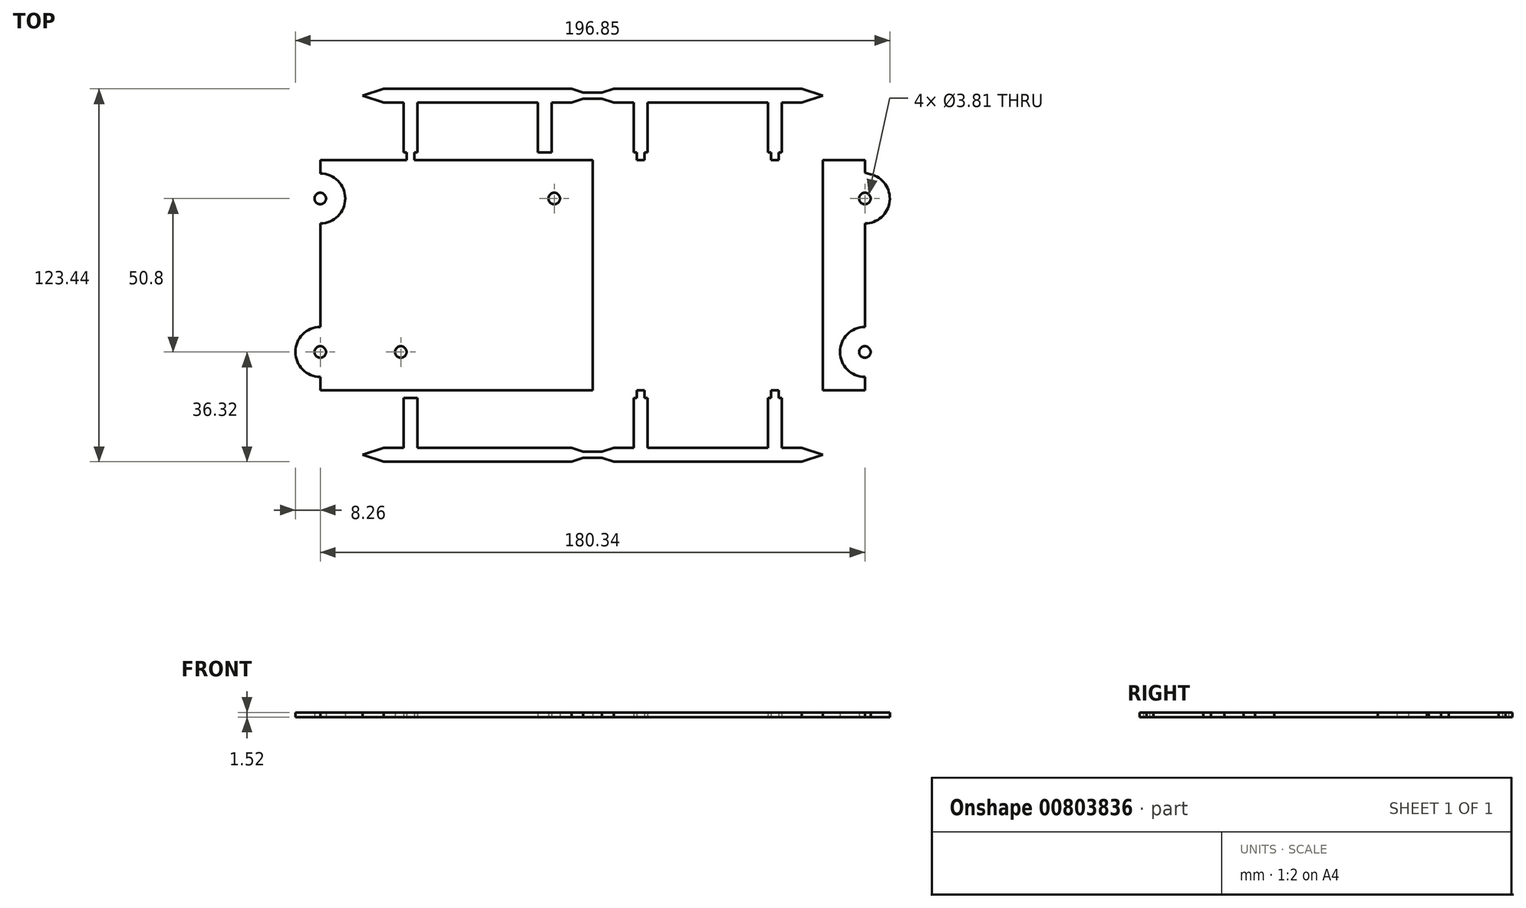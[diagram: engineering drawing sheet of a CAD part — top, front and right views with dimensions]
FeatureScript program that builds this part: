
annotation { "Feature Type Name" : "Feature", "Feature Type Description" : "" }
export const myFeature = defineFeature(function(context is Context, id is Id, definition is map)
    precondition{}
    {
        {
            var Q0;
            Q0=qCreatedBy(makeId("Top.planeOp"),FACE);
            var sketch = newSketch(context, id + "F0", { "sketchPlane" : qUnion([Q0])});
            skLineSegment(sketch, "E0.bottom", {"start": v(38.1, 38.1) * mm, "end": v(-38.1, 38.1) * mm});
            skLineSegment(sketch, "E0.top", {"start": v(38.1, -38.1) * mm, "end": v(-38.1, -38.1) * mm});
            skLineSegment(sketch, "E0.left", {"start": v(38.1, 38.1) * mm, "end": v(38.1, -38.1) * mm});
            skPoint(sketch, "E0.middle", {"position": v(0, 0) * mm});
            skLineSegment(sketch, "E1.bottom", {"start": v(31.75, 31.75) * mm, "end": v(-31.75, 31.75) * mm, "construction": true});
            skLineSegment(sketch, "E1.top", {"start": v(31.75, -31.75) * mm, "end": v(-31.75, -31.75) * mm, "construction": true});
            skLineSegment(sketch, "E1.left", {"start": v(31.75, 31.75) * mm, "end": v(31.75, -31.75) * mm, "construction": true});
            skLineSegment(sketch, "E1.right", {"start": v(-31.75, 31.75) * mm, "end": v(-31.75, -31.75) * mm, "construction": true});
            skLineSegment(sketch, "E2.bottom", {"start": v(-19.18, -31.75) * mm, "end": v(-12.57, -31.75) * mm});
            skLineSegment(sketch, "E2.top", {"start": v(-19.18, -30.23) * mm, "end": v(-12.57, -30.23) * mm});
            skLineSegment(sketch, "E2.left", {"start": v(-19.18, -31.75) * mm, "end": v(-19.18, -30.23) * mm});
            skLineSegment(sketch, "E2.right", {"start": v(-12.57, -31.75) * mm, "end": v(-12.57, -30.23) * mm});
            skPoint(sketch, "E3", {"position": v(-15.88, -31.75) * mm});
            skLineSegment(sketch, "E4.0", {"start": v(-19.43, -29.97) * mm, "end": v(-12.32, -29.97) * mm});
            skLineSegment(sketch, "E4.1", {"start": v(-19.43, -32) * mm, "end": v(-19.43, -29.97) * mm});
            skLineSegment(sketch, "E4.2", {"start": v(-19.43, -32) * mm, "end": v(-12.32, -32) * mm});
            skLineSegment(sketch, "E4.3", {"start": v(-12.32, -32) * mm, "end": v(-12.32, -29.97) * mm});
            skLineSegment(sketch, "E5.MirrorCS", {"start": v(19.43, -29.97) * mm, "end": v(12.32, -29.97) * mm});
            skLineSegment(sketch, "E6.MirrorCS", {"start": v(19.43, -32) * mm, "end": v(19.43, -29.97) * mm});
            skLineSegment(sketch, "E7.MirrorCS", {"start": v(19.43, -32) * mm, "end": v(12.32, -32) * mm});
            skLineSegment(sketch, "E8.MirrorCS", {"start": v(12.32, -32) * mm, "end": v(12.32, -29.97) * mm});
            skLineSegment(sketch, "E9.MirrorCS", {"start": v(-19.43, 32) * mm, "end": v(-19.43, 29.97) * mm});
            skLineSegment(sketch, "E10.MirrorCS", {"start": v(-19.43, 29.97) * mm, "end": v(-12.32, 29.97) * mm});
            skLineSegment(sketch, "E11.MirrorCS", {"start": v(-12.32, 32) * mm, "end": v(-12.32, 29.97) * mm});
            skLineSegment(sketch, "E12.MirrorCS", {"start": v(-19.43, 32) * mm, "end": v(-12.32, 32) * mm});
            skLineSegment(sketch, "E13.MirrorCS", {"start": v(19.43, 29.97) * mm, "end": v(12.32, 29.97) * mm});
            skLineSegment(sketch, "E14.MirrorCS", {"start": v(19.43, 32) * mm, "end": v(19.43, 29.97) * mm});
            skLineSegment(sketch, "E15.MirrorCS", {"start": v(19.43, 32) * mm, "end": v(12.32, 32) * mm});
            skLineSegment(sketch, "E16.MirrorCS", {"start": v(12.32, 32) * mm, "end": v(12.32, 29.97) * mm});
            skLineSegment(sketch, "E17.bottom", {"start": v(-31.75, -19.18) * mm, "end": v(-30.23, -19.18) * mm});
            skLineSegment(sketch, "E17.top", {"start": v(-31.75, -12.57) * mm, "end": v(-30.23, -12.57) * mm});
            skLineSegment(sketch, "E17.left", {"start": v(-31.75, -19.18) * mm, "end": v(-31.75, -12.57) * mm});
            skLineSegment(sketch, "E17.right", {"start": v(-30.23, -19.18) * mm, "end": v(-30.23, -12.57) * mm});
            skPoint(sketch, "E18", {"position": v(-31.75, -15.88) * mm});
            skLineSegment(sketch, "E19.0", {"start": v(-29.97, -19.43) * mm, "end": v(-29.97, -12.32) * mm});
            skLineSegment(sketch, "E19.1", {"start": v(-32, -19.43) * mm, "end": v(-29.97, -19.43) * mm});
            skLineSegment(sketch, "E19.2", {"start": v(-32, -19.43) * mm, "end": v(-32, -12.32) * mm});
            skLineSegment(sketch, "E19.3", {"start": v(-32, -12.32) * mm, "end": v(-29.97, -12.32) * mm});
            skLineSegment(sketch, "E20.MirrorCS", {"start": v(-32, 19.43) * mm, "end": v(-32, 12.32) * mm});
            skLineSegment(sketch, "E21.MirrorCS", {"start": v(-32, 12.32) * mm, "end": v(-29.97, 12.32) * mm});
            skLineSegment(sketch, "E22.MirrorCS", {"start": v(-29.97, 19.43) * mm, "end": v(-29.97, 12.32) * mm});
            skLineSegment(sketch, "E23.MirrorCS", {"start": v(-32, 19.43) * mm, "end": v(-29.97, 19.43) * mm});
            skLineSegment(sketch, "E24.MirrorCS", {"start": v(32, -19.43) * mm, "end": v(32, -12.32) * mm});
            skLineSegment(sketch, "E25.MirrorCS", {"start": v(32, -12.32) * mm, "end": v(29.97, -12.32) * mm});
            skLineSegment(sketch, "E26.MirrorCS", {"start": v(29.97, -19.43) * mm, "end": v(29.97, -12.32) * mm});
            skLineSegment(sketch, "E27.MirrorCS", {"start": v(32, -19.43) * mm, "end": v(29.97, -19.43) * mm});
            skLineSegment(sketch, "E28.MirrorCS", {"start": v(29.97, 19.43) * mm, "end": v(29.97, 12.32) * mm});
            skLineSegment(sketch, "E29.MirrorCS", {"start": v(32, 12.32) * mm, "end": v(29.97, 12.32) * mm});
            skLineSegment(sketch, "E30.MirrorCS", {"start": v(32, 19.43) * mm, "end": v(32, 12.32) * mm});
            skLineSegment(sketch, "E31.MirrorCS", {"start": v(32, 19.43) * mm, "end": v(29.97, 19.43) * mm});
            skLineSegment(sketch, "E32.bottom", {"start": v(-23.5, -38.1) * mm, "end": v(-20.96, -38.1) * mm});
            skLineSegment(sketch, "E32.top", {"start": v(-23.5, -40.64) * mm, "end": v(-20.96, -40.64) * mm});
            skLineSegment(sketch, "E32.left", {"start": v(-23.5, -38.1) * mm, "end": v(-23.5, -40.64) * mm});
            skLineSegment(sketch, "E32.right", {"start": v(-20.96, -38.1) * mm, "end": v(-20.96, -40.64) * mm});
            skPoint(sketch, "E33", {"position": v(-22.23, -38.1) * mm});
            skLineSegment(sketch, "E34.bottom", {"start": v(-24.51, -40.64) * mm, "end": v(-19.94, -40.64) * mm});
            skLineSegment(sketch, "E34.top", {"start": v(-24.51, -57.15) * mm, "end": v(-19.94, -57.15) * mm});
            skLineSegment(sketch, "E34.left", {"start": v(-24.51, -40.64) * mm, "end": v(-24.51, -57.15) * mm});
            skLineSegment(sketch, "E34.right", {"start": v(-19.94, -40.64) * mm, "end": v(-19.94, -57.15) * mm});
            skPoint(sketch, "E35", {"position": v(-22.23, -40.64) * mm});
            skLineSegment(sketch, "E36.MirrorCS", {"start": v(23.5, -38.1) * mm, "end": v(20.96, -38.1) * mm});
            skPoint(sketch, "E37.MirrorP", {"position": v(22.23, -38.1) * mm});
            skLineSegment(sketch, "E38.bottom", {"start": v(0, -57.15) * mm, "end": v(-31.12, -57.15) * mm});
            skLineSegment(sketch, "E38.top", {"start": v(0, -61.72) * mm, "end": v(-31.12, -61.72) * mm});
            skLineSegment(sketch, "E39", {"start": v(-38.1, -59.44) * mm, "end": v(-31.12, -57.15) * mm});
            skLineSegment(sketch, "E40", {"start": v(-38.1, -59.44) * mm, "end": v(-31.12, -61.72) * mm});
            skPoint(sketch, "E41.start.orphan", {"position": v(-31.12, -59.44) * mm});
            skLineSegment(sketch, "E42.MirrorCS", {"start": v(38.1, -38.1) * mm, "end": v(38.1, 38.1) * mm});
            skPoint(sketch, "E43.MirrorP", {"position": v(-38.1, 57.15) * mm});
            skCircle(sketch, "E44", {"center": v(-25.4, 25.4) * mm, "radius": 1.9 * mm});
            skCircle(sketch, "E45.MirrorC", {"center": v(25.4, 25.4) * mm, "radius": 1.9 * mm});
            skCircle(sketch, "E46.MirrorC", {"center": v(-25.4, -25.4) * mm, "radius": 1.9 * mm});
            skCircle(sketch, "E47.MirrorC", {"center": v(25.4, -25.4) * mm, "radius": 1.9 * mm});
            skLineSegment(sketch, "E48", {"start": v(0, 38.1) * mm, "end": v(0, -38.1) * mm, "construction": true});
            skLineSegment(sketch, "E49", {"start": v(0, -38.1) * mm, "end": v(0, -79.98) * mm, "construction": true});
            skLineSegment(sketch, "E50.MirrorCS", {"start": v(24.51, -40.64) * mm, "end": v(19.94, -40.64) * mm});
            skLineSegment(sketch, "E51.MirrorCS", {"start": v(23.5, -40.64) * mm, "end": v(20.96, -40.64) * mm});
            skLineSegment(sketch, "E52.MirrorCS", {"start": v(23.5, -38.1) * mm, "end": v(23.5, -40.64) * mm});
            skLineSegment(sketch, "E53.MirrorCS", {"start": v(20.96, -38.1) * mm, "end": v(20.96, -40.64) * mm});
            skLineSegment(sketch, "E54.MirrorCS", {"start": v(24.51, -57.15) * mm, "end": v(19.94, -57.15) * mm});
            skPoint(sketch, "E55.MirrorP", {"position": v(22.23, -40.64) * mm});
            skLineSegment(sketch, "E56.MirrorCS", {"start": v(0, -57.15) * mm, "end": v(31.12, -57.15) * mm});
            skLineSegment(sketch, "E57.MirrorCS", {"start": v(38.1, -59.44) * mm, "end": v(31.12, -57.15) * mm});
            skLineSegment(sketch, "E58.MirrorCS", {"start": v(38.1, -59.44) * mm, "end": v(31.12, -61.72) * mm});
            skLineSegment(sketch, "E59.MirrorCS", {"start": v(24.51, -40.64) * mm, "end": v(24.51, -57.15) * mm});
            skLineSegment(sketch, "E60.MirrorCS", {"start": v(0, -61.72) * mm, "end": v(31.12, -61.72) * mm});
            skPoint(sketch, "E61.MirrorP", {"position": v(31.12, -59.44) * mm});
            skLineSegment(sketch, "E62.MirrorCS", {"start": v(19.94, -40.64) * mm, "end": v(19.94, -57.15) * mm});
            skLineSegment(sketch, "E63.MirrorCS", {"start": v(-23.5, 40.64) * mm, "end": v(-20.96, 40.64) * mm});
            skLineSegment(sketch, "E64.MirrorCS", {"start": v(-24.51, 40.64) * mm, "end": v(-19.94, 40.64) * mm});
            skPoint(sketch, "E65.MirrorP", {"position": v(22.23, 38.1) * mm});
            skLineSegment(sketch, "E66.MirrorCS", {"start": v(24.51, 40.64) * mm, "end": v(19.94, 40.64) * mm});
            skLineSegment(sketch, "E67.MirrorCS", {"start": v(23.5, 40.64) * mm, "end": v(20.96, 40.64) * mm});
            skPoint(sketch, "E68.MirrorP", {"position": v(-22.23, 38.1) * mm});
            skPoint(sketch, "E69.MirrorP", {"position": v(22.23, 40.64) * mm});
            skPoint(sketch, "E70.MirrorP", {"position": v(-22.23, 40.64) * mm});
            skLineSegment(sketch, "E71.MirrorCS", {"start": v(24.51, 57.15) * mm, "end": v(19.94, 57.15) * mm});
            skLineSegment(sketch, "E72.MirrorCS", {"start": v(-24.51, 57.15) * mm, "end": v(-19.94, 57.15) * mm});
            skLineSegment(sketch, "E73.MirrorCS", {"start": v(24.51, 40.64) * mm, "end": v(24.51, 57.15) * mm});
            skLineSegment(sketch, "E74.MirrorCS", {"start": v(-24.51, 40.64) * mm, "end": v(-24.51, 57.15) * mm});
            skLineSegment(sketch, "E75.MirrorCS", {"start": v(-19.94, 40.64) * mm, "end": v(-19.94, 57.15) * mm});
            skLineSegment(sketch, "E76.MirrorCS", {"start": v(0, 61.72) * mm, "end": v(31.12, 61.72) * mm});
            skLineSegment(sketch, "E77.MirrorCS", {"start": v(-38.1, 59.44) * mm, "end": v(-31.12, 61.72) * mm});
            skLineSegment(sketch, "E78.MirrorCS", {"start": v(19.94, 40.64) * mm, "end": v(19.94, 57.15) * mm});
            skPoint(sketch, "E79.MirrorP", {"position": v(-31.12, 59.44) * mm});
            skLineSegment(sketch, "E80.MirrorCS", {"start": v(-38.1, 59.44) * mm, "end": v(-31.12, 57.15) * mm});
            skLineSegment(sketch, "E81.MirrorCS", {"start": v(0, 57.15) * mm, "end": v(31.12, 57.15) * mm});
            skLineSegment(sketch, "E82.MirrorCS", {"start": v(38.1, 59.44) * mm, "end": v(31.12, 61.72) * mm});
            skLineSegment(sketch, "E83.MirrorCS", {"start": v(0, 61.72) * mm, "end": v(-31.12, 61.72) * mm});
            skPoint(sketch, "E84.MirrorP", {"position": v(31.12, 59.44) * mm});
            skLineSegment(sketch, "E85.MirrorCS", {"start": v(0, 57.15) * mm, "end": v(-31.12, 57.15) * mm});
            skLineSegment(sketch, "E86.MirrorCS", {"start": v(38.1, 59.44) * mm, "end": v(31.12, 57.15) * mm});
            skLineSegment(sketch, "E87.MirrorCS", {"start": v(-23.5, 38.1) * mm, "end": v(-20.96, 38.1) * mm});
            skLineSegment(sketch, "E88.MirrorCS", {"start": v(-20.96, 38.1) * mm, "end": v(-20.96, 40.64) * mm});
            skLineSegment(sketch, "E89.MirrorCS", {"start": v(-23.5, 38.1) * mm, "end": v(-23.5, 40.64) * mm});
            skLineSegment(sketch, "E90.MirrorCS", {"start": v(23.5, 38.1) * mm, "end": v(20.96, 38.1) * mm});
            skLineSegment(sketch, "E91.MirrorCS", {"start": v(20.96, 38.1) * mm, "end": v(20.96, 40.64) * mm});
            skLineSegment(sketch, "E92.MirrorCS", {"start": v(23.5, 38.1) * mm, "end": v(23.5, 40.64) * mm});
            skLineSegment(sketch, "E93", {"start": v(-38.1, -59.44) * mm, "end": v(38.1, -59.44) * mm});
            skLineSegment(sketch, "E94.0", {"start": v(-38.1, -60.45) * mm, "end": v(38.1, -60.45) * mm});
            skLineSegment(sketch, "E95.0", {"start": v(-38.1, -58.42) * mm, "end": v(38.1, -58.42) * mm});
            skLineSegment(sketch, "E96.MirrorCS", {"start": v(-38.1, 58.42) * mm, "end": v(38.1, 58.42) * mm});
            skLineSegment(sketch, "E97.MirrorCS", {"start": v(-38.1, 60.45) * mm, "end": v(38.1, 60.45) * mm});
            skLineSegment(sketch, "E98.MirrorCS", {"start": v(52.7, 38.1) * mm, "end": v(55.25, 38.1) * mm});
            skLineSegment(sketch, "E99.MirrorCS", {"start": v(52.7, 40.64) * mm, "end": v(55.25, 40.64) * mm});
            skLineSegment(sketch, "E100.MirrorCS", {"start": v(52.7, 38.1) * mm, "end": v(52.7, 40.64) * mm});
            skLineSegment(sketch, "E101.MirrorCS", {"start": v(55.25, 38.1) * mm, "end": v(55.25, 40.64) * mm});
            skLineSegment(sketch, "E102.MirrorCS", {"start": v(99.7, 40.64) * mm, "end": v(97.16, 40.64) * mm});
            skLineSegment(sketch, "E103.MirrorCS", {"start": v(99.7, 38.1) * mm, "end": v(97.16, 38.1) * mm});
            skLineSegment(sketch, "E104.MirrorCS", {"start": v(97.16, 38.1) * mm, "end": v(97.16, 40.64) * mm});
            skLineSegment(sketch, "E105.MirrorCS", {"start": v(100.71, 40.64) * mm, "end": v(96.14, 40.64) * mm});
            skLineSegment(sketch, "E106.MirrorCS", {"start": v(99.7, 38.1) * mm, "end": v(99.7, 40.64) * mm});
            skLineSegment(sketch, "E107.MirrorCS", {"start": v(51.69, 40.64) * mm, "end": v(56.26, 40.64) * mm});
            skPoint(sketch, "E108.MirrorP", {"position": v(98.43, 38.1) * mm});
            skPoint(sketch, "E109.MirrorP", {"position": v(53.98, 40.64) * mm});
            skPoint(sketch, "E110.MirrorP", {"position": v(98.43, 40.64) * mm});
            skPoint(sketch, "E111.MirrorP", {"position": v(53.98, 38.1) * mm});
            skLineSegment(sketch, "E112.MirrorCS", {"start": v(38.1, 59.44) * mm, "end": v(45.08, 57.15) * mm});
            skLineSegment(sketch, "E113.MirrorCS", {"start": v(51.69, 57.15) * mm, "end": v(56.26, 57.15) * mm});
            skLineSegment(sketch, "E114.MirrorCS", {"start": v(100.71, 57.15) * mm, "end": v(96.14, 57.15) * mm});
            skLineSegment(sketch, "E115.MirrorCS", {"start": v(38.1, 59.44) * mm, "end": v(45.08, 61.72) * mm});
            skLineSegment(sketch, "E116.MirrorCS", {"start": v(114.3, 59.44) * mm, "end": v(107.32, 61.72) * mm});
            skLineSegment(sketch, "E117.MirrorCS", {"start": v(114.3, 59.44) * mm, "end": v(107.32, 57.15) * mm});
            skLineSegment(sketch, "E118.MirrorCS", {"start": v(38.1, 38.1) * mm, "end": v(114.3, 38.1) * mm});
            skLineSegment(sketch, "E119.MirrorCS", {"start": v(114.3, 60.45) * mm, "end": v(38.1, 60.45) * mm});
            skPoint(sketch, "E120.MirrorP", {"position": v(114.3, 57.15) * mm});
            skLineSegment(sketch, "E121.MirrorCS", {"start": v(76.2, 57.15) * mm, "end": v(45.08, 57.15) * mm});
            skPoint(sketch, "E122.MirrorP", {"position": v(107.32, 59.44) * mm});
            skPoint(sketch, "E123.MirrorP", {"position": v(45.08, 59.44) * mm});
            skLineSegment(sketch, "E124.MirrorCS", {"start": v(51.69, 40.64) * mm, "end": v(51.69, 57.15) * mm});
            skLineSegment(sketch, "E125.MirrorCS", {"start": v(100.71, 40.64) * mm, "end": v(100.71, 57.15) * mm});
            skLineSegment(sketch, "E126.MirrorCS", {"start": v(56.26, 40.64) * mm, "end": v(56.26, 57.15) * mm});
            skLineSegment(sketch, "E127.MirrorCS", {"start": v(96.14, 40.64) * mm, "end": v(96.14, 57.15) * mm});
            skLineSegment(sketch, "E128.MirrorCS", {"start": v(76.2, 61.72) * mm, "end": v(45.08, 61.72) * mm});
            skLineSegment(sketch, "E129.MirrorCS", {"start": v(76.2, 61.72) * mm, "end": v(107.32, 61.72) * mm});
            skLineSegment(sketch, "E130.MirrorCS", {"start": v(114.3, 58.42) * mm, "end": v(38.1, 58.42) * mm});
            skLineSegment(sketch, "E131.MirrorCS", {"start": v(76.2, 57.15) * mm, "end": v(107.32, 57.15) * mm});
            skLineSegment(sketch, "E132.MirrorCS", {"start": v(52.7, -38.1) * mm, "end": v(55.25, -38.1) * mm});
            skLineSegment(sketch, "E133.MirrorCS", {"start": v(52.7, -40.64) * mm, "end": v(55.25, -40.64) * mm});
            skLineSegment(sketch, "E134.MirrorCS", {"start": v(99.7, -38.1) * mm, "end": v(97.16, -38.1) * mm});
            skLineSegment(sketch, "E135.MirrorCS", {"start": v(55.25, -38.1) * mm, "end": v(55.25, -40.64) * mm});
            skLineSegment(sketch, "E136.MirrorCS", {"start": v(97.16, -38.1) * mm, "end": v(97.16, -40.64) * mm});
            skLineSegment(sketch, "E137.MirrorCS", {"start": v(52.7, -38.1) * mm, "end": v(52.7, -40.64) * mm});
            skLineSegment(sketch, "E138.MirrorCS", {"start": v(99.7, -40.64) * mm, "end": v(97.16, -40.64) * mm});
            skLineSegment(sketch, "E139.MirrorCS", {"start": v(99.7, -38.1) * mm, "end": v(99.7, -40.64) * mm});
            skLineSegment(sketch, "E140.MirrorCS", {"start": v(100.71, -40.64) * mm, "end": v(96.14, -40.64) * mm});
            skLineSegment(sketch, "E141.MirrorCS", {"start": v(51.69, -40.64) * mm, "end": v(56.26, -40.64) * mm});
            skLineSegment(sketch, "E142.MirrorCS", {"start": v(38.1, -59.44) * mm, "end": v(45.08, -61.72) * mm});
            skLineSegment(sketch, "E143.MirrorCS", {"start": v(114.3, -59.44) * mm, "end": v(107.32, -61.72) * mm});
            skLineSegment(sketch, "E144.MirrorCS", {"start": v(38.1, -59.44) * mm, "end": v(45.08, -57.15) * mm});
            skLineSegment(sketch, "E145.MirrorCS", {"start": v(51.69, -57.15) * mm, "end": v(56.26, -57.15) * mm});
            skLineSegment(sketch, "E146.MirrorCS", {"start": v(114.3, -59.44) * mm, "end": v(107.32, -57.15) * mm});
            skLineSegment(sketch, "E147.MirrorCS", {"start": v(100.71, -57.15) * mm, "end": v(96.14, -57.15) * mm});
            skPoint(sketch, "E148.MirrorP", {"position": v(98.42, -40.64) * mm});
            skPoint(sketch, "E149.MirrorP", {"position": v(53.97, -38.1) * mm});
            skPoint(sketch, "E150.MirrorP", {"position": v(53.97, -40.64) * mm});
            skLineSegment(sketch, "E151.MirrorCS", {"start": v(114.3, -59.44) * mm, "end": v(38.1, -59.44) * mm});
            skLineSegment(sketch, "E152.MirrorCS", {"start": v(100.71, -40.64) * mm, "end": v(100.71, -57.15) * mm});
            skLineSegment(sketch, "E153.MirrorCS", {"start": v(38.1, -38.1) * mm, "end": v(114.3, -38.1) * mm});
            skLineSegment(sketch, "E154.MirrorCS", {"start": v(96.14, -40.64) * mm, "end": v(96.14, -57.15) * mm});
            skLineSegment(sketch, "E155.MirrorCS", {"start": v(51.69, -40.64) * mm, "end": v(51.69, -57.15) * mm});
            skPoint(sketch, "E156.MirrorP", {"position": v(98.42, -38.1) * mm});
            skPoint(sketch, "E157.MirrorP", {"position": v(107.32, -59.44) * mm});
            skLineSegment(sketch, "E158.MirrorCS", {"start": v(76.2, -38.1) * mm, "end": v(76.2, -79.98) * mm, "construction": true});
            skPoint(sketch, "E159.MirrorP", {"position": v(92.08, -31.75) * mm});
            skLineSegment(sketch, "E160.MirrorCS", {"start": v(76.2, -61.72) * mm, "end": v(45.08, -61.72) * mm});
            skLineSegment(sketch, "E161.MirrorCS", {"start": v(76.2, -61.72) * mm, "end": v(107.32, -61.72) * mm});
            skLineSegment(sketch, "E162.MirrorCS", {"start": v(76.2, -57.15) * mm, "end": v(107.32, -57.15) * mm});
            skPoint(sketch, "E163.MirrorP", {"position": v(45.08, -59.44) * mm});
            skLineSegment(sketch, "E164.MirrorCS", {"start": v(56.26, -40.64) * mm, "end": v(56.26, -57.15) * mm});
            skLineSegment(sketch, "E165.MirrorCS", {"start": v(76.2, -57.15) * mm, "end": v(45.08, -57.15) * mm});
            skLineSegment(sketch, "E166.MirrorCS", {"start": v(114.3, -60.45) * mm, "end": v(38.1, -60.45) * mm});
            skLineSegment(sketch, "E167.MirrorCS", {"start": v(114.3, -58.42) * mm, "end": v(38.1, -58.42) * mm});
            skLineSegment(sketch, "E168", {"start": v(-38.1, 38.1) * mm, "end": v(-38.1, -38.1) * mm});
            skCircle(sketch, "E169", {"center": v(-52.07, -25.4) * mm, "radius": 1.9 * mm});
            skCircle(sketch, "E170.0", {"center": v(-52.07, -25.4) * mm, "radius": 8.25 * mm});
            skLineSegment(sketch, "E171", {"start": v(-38.1, -38.1) * mm, "end": v(-53.94, -33.44) * mm});
            skCircle(sketch, "E172.MirrorC", {"center": v(-52.07, 25.4) * mm, "radius": 1.9 * mm});
            skCircle(sketch, "E173.MirrorC", {"center": v(-52.07, 25.4) * mm, "radius": 8.25 * mm});
            skLineSegment(sketch, "E174.MirrorCS", {"start": v(-38.1, 38.1) * mm, "end": v(-53.94, 33.44) * mm});
            skLineSegment(sketch, "E175", {"start": v(-52.07, -17.14) * mm, "end": v(-52.07, 17.14) * mm});
            skCircle(sketch, "E176.MirrorC", {"center": v(128.27, -25.4) * mm, "radius": 1.9 * mm});
            skCircle(sketch, "E177.MirrorC", {"center": v(128.27, -25.4) * mm, "radius": 8.25 * mm});
            skCircle(sketch, "E178.MirrorC", {"center": v(128.27, 25.4) * mm, "radius": 1.9 * mm});
            skLineSegment(sketch, "E179.MirrorCS", {"start": v(114.3, 38.1) * mm, "end": v(130.14, 33.44) * mm});
            skCircle(sketch, "E180.MirrorC", {"center": v(128.27, 25.4) * mm, "radius": 8.25 * mm});
            skLineSegment(sketch, "E181.MirrorCS", {"start": v(114.3, 38.1) * mm, "end": v(114.3, -38.1) * mm});
            skLineSegment(sketch, "E182.MirrorCS", {"start": v(114.3, -38.1) * mm, "end": v(130.14, -33.44) * mm});
            skLineSegment(sketch, "E183.MirrorCS", {"start": v(128.27, -17.15) * mm, "end": v(128.27, 17.14) * mm});
            skLineSegment(sketch, "E184", {"start": v(-52.07, -33.65) * mm, "end": v(-52.07, -38.1) * mm});
            skLineSegment(sketch, "E185", {"start": v(-52.07, -38.1) * mm, "end": v(-38.1, -38.1) * mm});
            skLineSegment(sketch, "E186.MirrorCS", {"start": v(-52.07, 38.1) * mm, "end": v(-38.1, 38.1) * mm});
            skLineSegment(sketch, "E187.MirrorCS", {"start": v(-52.07, 33.65) * mm, "end": v(-52.07, 38.1) * mm});
            skLineSegment(sketch, "E188.MirrorCS", {"start": v(128.27, 33.65) * mm, "end": v(128.27, 38.1) * mm});
            skLineSegment(sketch, "E189.MirrorCS", {"start": v(128.27, 38.1) * mm, "end": v(114.3, 38.1) * mm});
            skLineSegment(sketch, "E190.MirrorCS", {"start": v(128.27, -38.1) * mm, "end": v(114.3, -38.1) * mm});
            skLineSegment(sketch, "E191.MirrorCS", {"start": v(128.27, -33.66) * mm, "end": v(128.27, -38.1) * mm});
            skSolve(sketch);
        }
        {
            var Q0;
            {var subQ1=sQuery(id+"F0.wireOp",EDGE,"E74.MirrorCS");Q0=makeQuery(id+"F0.imprint","IMPRINT",FACE,{"disambiguationData":[TD([[makeQuery(id+"F0.imprint","IMPRINT",EDGE,{"derivedFrom":subQ1}),-1.0]])]});}
            var Q1;
            {var subQ1=sQuery(id+"F0.wireOp",EDGE,"E121.MirrorCS");var subQ9=sQuery(id+"F0.wireOp",EDGE,"E112.MirrorCS");var subQ10=makeQuery(id+"F0.imprint","INTERSECT",VERTEX,{"derivedFrom":[subQ9,subQ1]});Q1=makeQuery(id+"F0.imprint","IMPRINT",FACE,{"disambiguationData":[TD([[makeQuery(id+"F0.imprint","IMPRINT",EDGE,{"disambiguationData":[TD([[subQ10,1.0]])],"derivedFrom":subQ9}),1.0]])]});}
            var Q2;
            {var subQ5=sQuery(id+"F0.wireOp",EDGE,"E85.MirrorCS");var subQ7=sQuery(id+"F0.wireOp",EDGE,"E80.MirrorCS");var subQ8=makeQuery(id+"F0.imprint","INTERSECT",VERTEX,{"derivedFrom":[subQ7,subQ5]});Q2=makeQuery(id+"F0.imprint","IMPRINT",FACE,{"disambiguationData":[TD([[makeQuery(id+"F0.imprint","IMPRINT",EDGE,{"disambiguationData":[TD([[subQ8,1.0]])],"derivedFrom":subQ7}),1.0]])]});}
            var Q3;
            {var subQ0=sQuery(id+"F0.wireOp",EDGE,"E128.MirrorCS");Q3=makeQuery(id+"F0.imprint","IMPRINT",FACE,{"disambiguationData":[TD([[makeQuery(id+"F0.imprint","IMPRINT",EDGE,{"derivedFrom":subQ0}),1.0]])]});}
            var Q4;
            {var subQ1=sQuery(id+"F0.wireOp",EDGE,"E76.MirrorCS");Q4=makeQuery(id+"F0.imprint","IMPRINT",FACE,{"disambiguationData":[TD([[makeQuery(id+"F0.imprint","IMPRINT",EDGE,{"derivedFrom":subQ1}),-1.0]])]});}
            var Q5;
            {var subQ5=sQuery(id+"F0.wireOp",EDGE,"E80.MirrorCS");var subQ6=sQuery(id+"F0.wireOp",EDGE,"E77.MirrorCS");var subQ7=makeQuery(id+"F0.imprint","INTERSECT",VERTEX,{"derivedFrom":[subQ6,subQ5]});Q5=makeQuery(id+"F0.imprint","IMPRINT",FACE,{"disambiguationData":[TD([[makeQuery(id+"F0.imprint","IMPRINT",EDGE,{"disambiguationData":[TD([[subQ7,-1.0]])],"derivedFrom":subQ6}),-1.0]])]});}
            var Q6;
            {var subQ3=sQuery(id+"F0.wireOp",EDGE,"E97.MirrorCS");var subQ5=sQuery(id+"F0.wireOp",EDGE,"E119.MirrorCS");var subQ6=makeQuery(id+"F0.imprint","INTERSECT",VERTEX,{"derivedFrom":[subQ3,subQ5]});Q6=makeQuery(id+"F0.imprint","IMPRINT",FACE,{"disambiguationData":[TD([[makeQuery(id+"F0.imprint","IMPRINT",EDGE,{"disambiguationData":[TD([[subQ6,1.0]])],"derivedFrom":subQ3}),-1.0]])]});}
            var Q7;
            {var subQ0=sQuery(id+"F0.wireOp",EDGE,"E117.MirrorCS");var subQ1=sQuery(id+"F0.wireOp",EDGE,"E116.MirrorCS");var subQ2=makeQuery(id+"F0.imprint","INTERSECT",VERTEX,{"derivedFrom":[subQ1,subQ0]});Q7=makeQuery(id+"F0.imprint","IMPRINT",FACE,{"disambiguationData":[TD([[makeQuery(id+"F0.imprint","IMPRINT",EDGE,{"disambiguationData":[TD([[subQ2,-1.0]])],"derivedFrom":subQ1}),1.0]])]});}
            var Q8;
            {var subQ3=sQuery(id+"F0.wireOp",EDGE,"E96.MirrorCS");var subQ5=sQuery(id+"F0.wireOp",EDGE,"E130.MirrorCS");var subQ6=makeQuery(id+"F0.imprint","INTERSECT",VERTEX,{"derivedFrom":[subQ3,subQ5]});Q8=makeQuery(id+"F0.imprint","IMPRINT",FACE,{"disambiguationData":[TD([[makeQuery(id+"F0.imprint","IMPRINT",EDGE,{"disambiguationData":[TD([[subQ6,1.0]])],"derivedFrom":subQ3}),1.0]])]});}
            var Q9;
            {var subQ1=sQuery(id+"F0.wireOp",EDGE,"E73.MirrorCS");Q9=makeQuery(id+"F0.imprint","IMPRINT",FACE,{"disambiguationData":[TD([[makeQuery(id+"F0.imprint","IMPRINT",EDGE,{"derivedFrom":subQ1}),1.0]])]});}
            var Q10;
            {var subQ0=sQuery(id+"F0.wireOp",EDGE,"E124.MirrorCS");Q10=makeQuery(id+"F0.imprint","IMPRINT",FACE,{"disambiguationData":[TD([[makeQuery(id+"F0.imprint","IMPRINT",EDGE,{"derivedFrom":subQ0}),-1.0]])]});}
            var Q11;
            {var subQ4=sQuery(id+"F0.wireOp",EDGE,"E125.MirrorCS");Q11=makeQuery(id+"F0.imprint","IMPRINT",FACE,{"disambiguationData":[TD([[makeQuery(id+"F0.imprint","IMPRINT",EDGE,{"derivedFrom":subQ4}),1.0]])]});}
            var Q12;
            Q12=makeQuery(id+"F0.imprint","IMPRINT",FACE,{"disambiguationData":[TD([[makeQuery(id+"F0.imprint","IMPRINT",EDGE,{"derivedFrom":sQuery(id+"F0.wireOp",EDGE,"E63.MirrorCS")}),-1.0]])]});
            var Q13;
            {var subQ0=sQuery(id+"F0.wireOp",EDGE,"E104.MirrorCS");Q13=makeQuery(id+"F0.imprint","IMPRINT",FACE,{"disambiguationData":[TD([[makeQuery(id+"F0.imprint","IMPRINT",EDGE,{"derivedFrom":subQ0}),-1.0]])]});}
            var Q14;
            Q14=makeQuery(id+"F0.imprint","IMPRINT",FACE,{"disambiguationData":[TD([[makeQuery(id+"F0.imprint","IMPRINT",EDGE,{"derivedFrom":sQuery(id+"F0.wireOp",EDGE,"E90.MirrorCS")}),-1.0]])]});
            var Q15;
            {var subQ0=sQuery(id+"F0.wireOp",EDGE,"E100.MirrorCS");Q15=makeQuery(id+"F0.imprint","IMPRINT",FACE,{"disambiguationData":[TD([[makeQuery(id+"F0.imprint","IMPRINT",EDGE,{"derivedFrom":subQ0}),-1.0]])]});}
            var Q16;
            {var subQ8=sQuery(id+"F0.wireOp",EDGE,"E42.MirrorCS");Q16=makeQuery(id+"F0.imprint","IMPRINT",FACE,{"disambiguationData":[TD([[makeQuery(id+"F0.imprint","IMPRINT",EDGE,{"derivedFrom":subQ8}),-1.0]])]});}
            var Q17;
            Q17=makeQuery(id+"F0.imprint","IMPRINT",FACE,{"disambiguationData":[TD([[makeQuery(id+"F0.imprint","IMPRINT",EDGE,{"derivedFrom":sQuery(id+"F0.wireOp",EDGE,"70d0816f-e94a-49aa-9acb-d33a838f75eb1.MirrorC")}),-1.0]])]});
            var Q18;
            Q18=makeQuery(id+"F0.imprint","IMPRINT",FACE,{"disambiguationData":[TD([[makeQuery(id+"F0.imprint","IMPRINT",EDGE,{"derivedFrom":sQuery(id+"F0.wireOp",EDGE,"70d0816f-e94a-49aa-9acb-d33a838f75eb0.MirrorC")}),1.0]])]});
            var Q19;
            {var subQ4=sQuery(id+"F0.wireOp",EDGE,"70d0816f-e94a-49aa-9acb-d33a838f75eb3.MirrorCS");Q19=makeQuery(id+"F0.imprint","IMPRINT",FACE,{"disambiguationData":[TD([[makeQuery(id+"F0.imprint","IMPRINT",EDGE,{"derivedFrom":subQ4}),1.0]])]});}
            var Q20;
            {var subQ4=sQuery(id+"F0.wireOp",EDGE,"E152.MirrorCS");Q20=makeQuery(id+"F0.imprint","IMPRINT",FACE,{"disambiguationData":[TD([[makeQuery(id+"F0.imprint","IMPRINT",EDGE,{"derivedFrom":subQ4}),-1.0]])]});}
            var Q21;
            {var subQ0=sQuery(id+"F0.wireOp",EDGE,"E155.MirrorCS");Q21=makeQuery(id+"F0.imprint","IMPRINT",FACE,{"disambiguationData":[TD([[makeQuery(id+"F0.imprint","IMPRINT",EDGE,{"derivedFrom":subQ0}),1.0]])]});}
            var Q22;
            {var subQ0=sQuery(id+"F0.wireOp",EDGE,"E151.MirrorCS");Q22=makeQuery(id+"F0.imprint","IMPRINT",FACE,{"disambiguationData":[TD([[makeQuery(id+"F0.imprint","IMPRINT",EDGE,{"derivedFrom":subQ0}),-1.0]])]});}
            var Q23;
            {var subQ0=sQuery(id+"F0.wireOp",EDGE,"E160.MirrorCS");Q23=makeQuery(id+"F0.imprint","IMPRINT",FACE,{"disambiguationData":[TD([[makeQuery(id+"F0.imprint","IMPRINT",EDGE,{"derivedFrom":subQ0}),-1.0]])]});}
            var Q24;
            {var subQ2=sQuery(id+"F0.wireOp",EDGE,"E165.MirrorCS");var subQ9=sQuery(id+"F0.wireOp",EDGE,"E144.MirrorCS");var subQ10=makeQuery(id+"F0.imprint","INTERSECT",VERTEX,{"derivedFrom":[subQ9,subQ2]});Q24=makeQuery(id+"F0.imprint","IMPRINT",FACE,{"disambiguationData":[TD([[makeQuery(id+"F0.imprint","IMPRINT",EDGE,{"disambiguationData":[TD([[subQ10,1.0]])],"derivedFrom":subQ9}),-1.0]])]});}
            var Q25;
            {var subQ0=sQuery(id+"F0.wireOp",EDGE,"E151.MirrorCS");Q25=makeQuery(id+"F0.imprint","IMPRINT",FACE,{"disambiguationData":[TD([[makeQuery(id+"F0.imprint","IMPRINT",EDGE,{"derivedFrom":subQ0}),1.0]])]});}
            var Q26;
            {var subQ0=sQuery(id+"F0.wireOp",EDGE,"E136.MirrorCS");Q26=makeQuery(id+"F0.imprint","IMPRINT",FACE,{"disambiguationData":[TD([[makeQuery(id+"F0.imprint","IMPRINT",EDGE,{"derivedFrom":subQ0}),1.0]])]});}
            var Q27;
            {var subQ0=sQuery(id+"F0.wireOp",EDGE,"E135.MirrorCS");Q27=makeQuery(id+"F0.imprint","IMPRINT",FACE,{"disambiguationData":[TD([[makeQuery(id+"F0.imprint","IMPRINT",EDGE,{"derivedFrom":subQ0}),-1.0]])]});}
            var Q28;
            {var subQ3=sQuery(id+"F0.wireOp",EDGE,"E51.MirrorCS");Q28=makeQuery(id+"F0.imprint","IMPRINT",FACE,{"disambiguationData":[TD([[makeQuery(id+"F0.imprint","IMPRINT",EDGE,{"derivedFrom":subQ3}),1.0]])]});}
            var Q29;
            {var subQ0=sQuery(id+"F0.wireOp",EDGE,"E34.left");Q29=makeQuery(id+"F0.imprint","IMPRINT",FACE,{"disambiguationData":[TD([[makeQuery(id+"F0.imprint","IMPRINT",EDGE,{"derivedFrom":subQ0}),1.0]])]});}
            var Q30;
            {var subQ0=sQuery(id+"F0.wireOp",EDGE,"E93");Q30=makeQuery(id+"F0.imprint","IMPRINT",FACE,{"disambiguationData":[TD([[makeQuery(id+"F0.imprint","IMPRINT",EDGE,{"derivedFrom":subQ0}),1.0]])]});}
            var Q31;
            {var subQ0=sQuery(id+"F0.wireOp",EDGE,"E38.bottom");var subQ11=makeQuery(id+"F0.imprint","INTERSECT",VERTEX,{"derivedFrom":[sQuery(id+"F0.wireOp",EDGE,"E34.right"),subQ0]});Q31=makeQuery(id+"F0.imprint","IMPRINT",FACE,{"disambiguationData":[TD([[makeQuery(id+"F0.imprint","IMPRINT",EDGE,{"disambiguationData":[TD([[subQ11,1.0]])],"derivedFrom":subQ0}),1.0]])]});}
            var Q32;
            {var subQ5=sQuery(id+"F0.wireOp",EDGE,"E38.top");Q32=makeQuery(id+"F0.imprint","IMPRINT",FACE,{"disambiguationData":[TD([[makeQuery(id+"F0.imprint","IMPRINT",EDGE,{"derivedFrom":subQ5}),-1.0]])]});}
            var Q33;
            {var subQ0=sQuery(id+"F0.wireOp",EDGE,"E93");Q33=makeQuery(id+"F0.imprint","IMPRINT",FACE,{"disambiguationData":[TD([[makeQuery(id+"F0.imprint","IMPRINT",EDGE,{"derivedFrom":subQ0}),-1.0]])]});}
            var Q34;
            {var subQ3=sQuery(id+"F0.wireOp",EDGE,"E95.0");var subQ5=sQuery(id+"F0.wireOp",EDGE,"E167.MirrorCS");var subQ6=makeQuery(id+"F0.imprint","INTERSECT",VERTEX,{"derivedFrom":[subQ3,subQ5]});Q34=makeQuery(id+"F0.imprint","IMPRINT",FACE,{"disambiguationData":[TD([[makeQuery(id+"F0.imprint","IMPRINT",EDGE,{"disambiguationData":[TD([[subQ6,1.0]])],"derivedFrom":subQ3}),-1.0]])]});}
            var Q35;
            {var subQ3=sQuery(id+"F0.wireOp",EDGE,"E94.0");var subQ5=sQuery(id+"F0.wireOp",EDGE,"E166.MirrorCS");var subQ7=makeQuery(id+"F0.imprint","INTERSECT",VERTEX,{"derivedFrom":[subQ3,subQ5]});Q35=makeQuery(id+"F0.imprint","IMPRINT",FACE,{"disambiguationData":[TD([[makeQuery(id+"F0.imprint","IMPRINT",EDGE,{"disambiguationData":[TD([[subQ7,1.0]])],"derivedFrom":subQ3}),1.0]])]});}
            var Q36;
            Q36=makeQuery(id+"F0.imprint","IMPRINT",FACE,{"disambiguationData":[TD([[makeQuery(id+"F0.imprint","IMPRINT",EDGE,{"derivedFrom":sQuery(id+"F0.wireOp",EDGE,"E32.bottom")}),-1.0]])]});
            var Q37;
            Q37=makeQuery(id+"F0.imprint","IMPRINT",FACE,{"disambiguationData":[TD([[makeQuery(id+"F0.imprint","IMPRINT",EDGE,{"derivedFrom":sQuery(id+"F0.wireOp",EDGE,"E51.MirrorCS")}),-1.0]])]});
            var Q38;
            Q38=makeQuery(id+"F0.imprint","IMPRINT",FACE,{"disambiguationData":[TD([[makeQuery(id+"F0.imprint","IMPRINT",EDGE,{"derivedFrom":sQuery(id+"F0.wireOp",EDGE,"52253c02-b3a7-4167-a365-0132d2a085360.MirrorC")}),-1.0]])]});
            var Q39;
            Q39=makeQuery(id+"F0.imprint","IMPRINT",FACE,{"disambiguationData":[TD([[makeQuery(id+"F0.imprint","IMPRINT",EDGE,{"derivedFrom":sQuery(id+"F0.wireOp",EDGE,"E13.MirrorCS")}),-1.0]])]});
            var Q40;
            Q40=makeQuery(id+"F0.imprint","IMPRINT",FACE,{"disambiguationData":[TD([[makeQuery(id+"F0.imprint","IMPRINT",EDGE,{"derivedFrom":sQuery(id+"F0.wireOp",EDGE,"9be87093-70ac-4365-98c4-c9c937672a0f0.MirrorC")}),1.0]])]});
            var Q41;
            Q41=makeQuery(id+"F0.imprint","IMPRINT",FACE,{"disambiguationData":[TD([[makeQuery(id+"F0.imprint","IMPRINT",EDGE,{"derivedFrom":sQuery(id+"F0.wireOp",EDGE,"E5.MirrorCS")}),1.0]])]});
            var Q42;
            Q42=makeQuery(id+"F0.imprint","IMPRINT",FACE,{"disambiguationData":[TD([[makeQuery(id+"F0.imprint","IMPRINT",EDGE,{"derivedFrom":sQuery(id+"F0.wireOp",EDGE,"E9.MirrorCS")}),1.0]])]});
            var Q43;
            Q43=makeQuery(id+"F0.imprint","IMPRINT",FACE,{"disambiguationData":[TD([[makeQuery(id+"F0.imprint","IMPRINT",EDGE,{"derivedFrom":sQuery(id+"F0.wireOp",EDGE,"E20.MirrorCS")}),1.0]])]});
            var Q44;
            Q44=makeQuery(id+"F0.imprint","IMPRINT",FACE,{"disambiguationData":[TD([[makeQuery(id+"F0.imprint","IMPRINT",EDGE,{"derivedFrom":sQuery(id+"F0.wireOp",EDGE,"E24.MirrorCS")}),1.0]])]});
            var Q45;
            Q45=makeQuery(id+"F0.imprint","IMPRINT",FACE,{"disambiguationData":[TD([[makeQuery(id+"F0.imprint","IMPRINT",EDGE,{"derivedFrom":sQuery(id+"F0.wireOp",EDGE,"E28.MirrorCS")}),1.0]])]});
            var Q46;
            Q46=makeQuery(id+"F0.imprint","IMPRINT",FACE,{"disambiguationData":[TD([[makeQuery(id+"F0.imprint","IMPRINT",EDGE,{"derivedFrom":sQuery(id+"F0.wireOp",EDGE,"E4.0")}),1.0]])]});
            var Q47;
            Q47=makeQuery(id+"F0.imprint","IMPRINT",FACE,{"disambiguationData":[TD([[makeQuery(id+"F0.imprint","IMPRINT",EDGE,{"derivedFrom":sQuery(id+"F0.wireOp",EDGE,"53851779-1c45-4308-9c8f-5f77561e0c2317.MirrorCS")}),1.0]])]});
            var Q48;
            Q48=makeQuery(id+"F0.imprint","IMPRINT",FACE,{"disambiguationData":[TD([[makeQuery(id+"F0.imprint","IMPRINT",EDGE,{"derivedFrom":sQuery(id+"F0.wireOp",EDGE,"E2.bottom")}),1.0]])]});
            var Q49;
            Q49=makeQuery(id+"F0.imprint","IMPRINT",FACE,{"disambiguationData":[TD([[makeQuery(id+"F0.imprint","IMPRINT",EDGE,{"derivedFrom":sQuery(id+"F0.wireOp",EDGE,"E44")}),1.0]])]});
            var Q50;
            Q50=makeQuery(id+"F0.imprint","IMPRINT",FACE,{"disambiguationData":[TD([[makeQuery(id+"F0.imprint","IMPRINT",EDGE,{"derivedFrom":sQuery(id+"F0.wireOp",EDGE,"E45.MirrorC")}),-1.0]])]});
            var Q51;
            Q51=makeQuery(id+"F0.imprint","IMPRINT",FACE,{"disambiguationData":[TD([[makeQuery(id+"F0.imprint","IMPRINT",EDGE,{"derivedFrom":sQuery(id+"F0.wireOp",EDGE,"E46.MirrorC")}),-1.0]])]});
            var Q52;
            Q52=makeQuery(id+"F0.imprint","IMPRINT",FACE,{"disambiguationData":[TD([[makeQuery(id+"F0.imprint","IMPRINT",EDGE,{"derivedFrom":sQuery(id+"F0.wireOp",EDGE,"E47.MirrorC")}),1.0]])]});
            var Q53;
            Q53=makeQuery(id+"F0.imprint","IMPRINT",FACE,{"disambiguationData":[TD([[makeQuery(id+"F0.imprint","IMPRINT",EDGE,{"derivedFrom":sQuery(id+"F0.wireOp",EDGE,"E17.bottom")}),1.0]])]});
            var Q54;
            Q54=makeQuery(id+"F0.imprint","IMPRINT",FACE,{"disambiguationData":[TD([[makeQuery(id+"F0.imprint","IMPRINT",EDGE,{"derivedFrom":sQuery(id+"F0.wireOp",EDGE,"E17.bottom")}),-1.0]])]});
            var Q55;
            Q55=makeQuery(id+"F0.imprint","IMPRINT",FACE,{"disambiguationData":[TD([[makeQuery(id+"F0.imprint","IMPRINT",EDGE,{"derivedFrom":sQuery(id+"F0.wireOp",EDGE,"E2.bottom")}),-1.0]])]});
            var Q56;
            {var subQ1=sQuery(id+"F0.wireOp",EDGE,"70d0816f-e94a-49aa-9acb-d33a838f75eb5.MirrorCS");Q56=makeQuery(id+"F0.imprint","IMPRINT",FACE,{"disambiguationData":[TD([[makeQuery(id+"F0.imprint","IMPRINT",EDGE,{"derivedFrom":subQ1}),1.0]])]});}
            var Q57;
            Q57=makeQuery(id+"F0.imprint","IMPRINT",FACE,{"disambiguationData":[TD([[makeQuery(id+"F0.imprint","IMPRINT",EDGE,{"derivedFrom":sQuery(id+"F0.wireOp",EDGE,"70d0816f-e94a-49aa-9acb-d33a838f75eb8.MirrorCS")}),1.0]])]});
            var Q58;
            Q58=makeQuery(id+"F0.imprint","IMPRINT",FACE,{"disambiguationData":[TD([[makeQuery(id+"F0.imprint","IMPRINT",EDGE,{"derivedFrom":sQuery(id+"F0.wireOp",EDGE,"E168")}),-1.0]])]});
            var Q59;
            Q59=makeQuery(id+"F0.imprint","IMPRINT",FACE,{"disambiguationData":[TD([[makeQuery(id+"F0.imprint","IMPRINT",EDGE,{"derivedFrom":sQuery(id+"F0.wireOp",EDGE,"E172.MirrorC")}),1.0]])]});
            var Q60;
            Q60=makeQuery(id+"F0.imprint","IMPRINT",FACE,{"disambiguationData":[TD([[makeQuery(id+"F0.imprint","IMPRINT",EDGE,{"derivedFrom":sQuery(id+"F0.wireOp",EDGE,"E169")}),-1.0]])]});
            var Q61;
            {var subQ1=sQuery(id+"F0.wireOp",EDGE,"E179.MirrorCS");Q61=makeQuery(id+"F0.imprint","IMPRINT",FACE,{"disambiguationData":[TD([[makeQuery(id+"F0.imprint","IMPRINT",EDGE,{"derivedFrom":subQ1}),-1.0]])]});}
            var Q62;
            Q62=makeQuery(id+"F0.imprint","IMPRINT",FACE,{"disambiguationData":[TD([[makeQuery(id+"F0.imprint","IMPRINT",EDGE,{"derivedFrom":sQuery(id+"F0.wireOp",EDGE,"E176.MirrorC")}),1.0]])]});
            var Q63;
            Q63=makeQuery(id+"F0.imprint","IMPRINT",FACE,{"disambiguationData":[TD([[makeQuery(id+"F0.imprint","IMPRINT",EDGE,{"derivedFrom":sQuery(id+"F0.wireOp",EDGE,"E178.MirrorC")}),-1.0]])]});
            var Q64;
            {var subQ6=sQuery(id+"F0.wireOp",EDGE,"E181.MirrorCS");Q64=makeQuery(id+"F0.imprint","IMPRINT",FACE,{"disambiguationData":[TD([[makeQuery(id+"F0.imprint","IMPRINT",EDGE,{"derivedFrom":subQ6}),1.0]])]});}
            var Q65;
            {var subQ0=sQuery(id+"F0.wireOp",EDGE,"E189.MirrorCS");Q65=makeQuery(id+"F0.imprint","IMPRINT",FACE,{"disambiguationData":[TD([[makeQuery(id+"F0.imprint","IMPRINT",EDGE,{"derivedFrom":subQ0}),1.0]])]});}
            var Q66;
            {var subQ0=sQuery(id+"F0.wireOp",EDGE,"E190.MirrorCS");Q66=makeQuery(id+"F0.imprint","IMPRINT",FACE,{"disambiguationData":[TD([[makeQuery(id+"F0.imprint","IMPRINT",EDGE,{"derivedFrom":subQ0}),-1.0]])]});}
            var Q67;
            {var subQ0=sQuery(id+"F0.wireOp",EDGE,"E186.MirrorCS");Q67=makeQuery(id+"F0.imprint","IMPRINT",FACE,{"disambiguationData":[TD([[makeQuery(id+"F0.imprint","IMPRINT",EDGE,{"derivedFrom":subQ0}),-1.0]])]});}
            var Q68;
            {var subQ0=sQuery(id+"F0.wireOp",EDGE,"E185");Q68=makeQuery(id+"F0.imprint","IMPRINT",FACE,{"disambiguationData":[TD([[makeQuery(id+"F0.imprint","IMPRINT",EDGE,{"derivedFrom":subQ0}),1.0]])]});}
            extrude(context, id + "F1", {"entities" : qUnion([Q0, Q1, Q2, Q3, Q4, Q5, Q6, Q7, Q8, Q9, Q10, Q11, Q12, Q13, Q14, Q15, Q16, Q17, Q18, Q19, Q20, Q21, Q22, Q23, Q24, Q25, Q26, Q27, Q28, Q29, Q30, Q31, Q32, Q33, Q34, Q35, Q36, Q37, Q38, Q39, Q40, Q41, Q42, Q43, Q44, Q45, Q46, Q47, Q48, Q49, Q50, Q51, Q52, Q53, Q54, Q55, Q56, Q57, Q58, Q59, Q60, Q61, Q62, Q63, Q64, Q65, Q66, Q67, Q68]), "depth" : 1.52 * mm, "offsetDistance" : 25.4 * mm});
        }
    });
